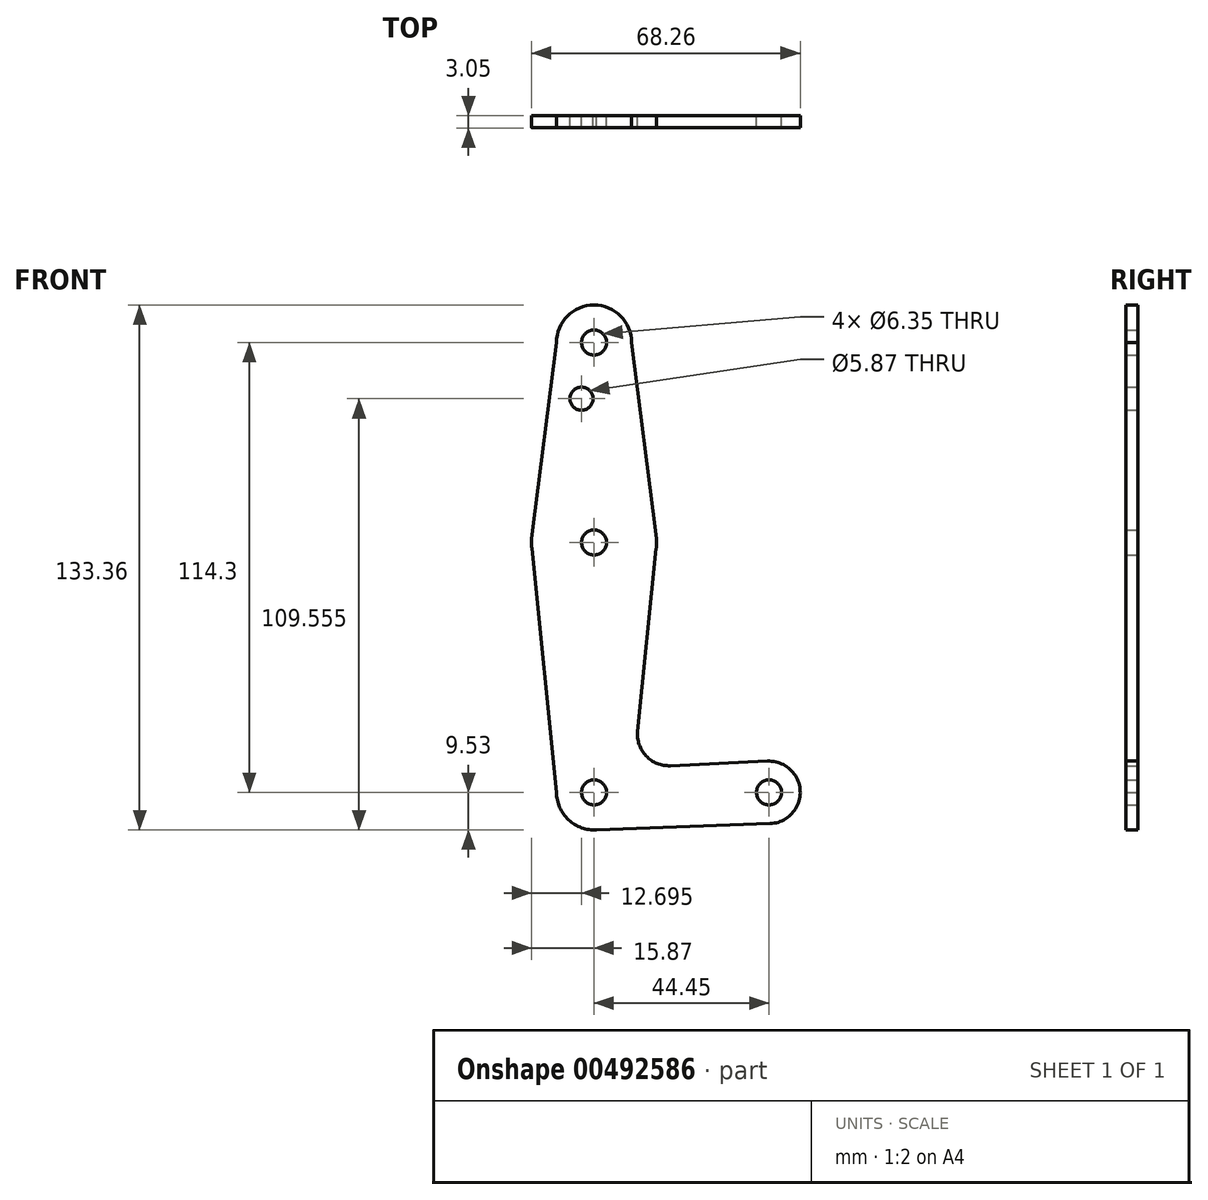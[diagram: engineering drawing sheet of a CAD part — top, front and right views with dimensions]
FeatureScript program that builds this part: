
annotation { "Feature Type Name" : "Feature", "Feature Type Description" : "" }
export const myFeature = defineFeature(function(context is Context, id is Id, definition is map)
    precondition{}
    {
        {
            var Q0;
            Q0=qCreatedBy(makeId("Front.planeOp"),FACE);
            var sketch = newSketch(context, id + "F0", { "sketchPlane" : qUnion([Q0])});
            skLineSegment(sketch, "E0", {"start": v(0, 0) * mm, "end": v(44.45, 0) * mm, "construction": true});
            skCircle(sketch, "E1", {"center": v(0, 0) * mm, "radius": 9.53 * mm});
            skCircle(sketch, "E2", {"center": v(44.45, 0) * mm, "radius": 7.94 * mm});
            skLineSegment(sketch, "E3", {"start": v(0, 0) * mm, "end": v(0, 114.3) * mm, "construction": true});
            skCircle(sketch, "E4", {"center": v(0, 114.3) * mm, "radius": 9.53 * mm});
            skCircle(sketch, "E5", {"center": v(0, 63.5) * mm, "radius": 15.88 * mm});
            skLineSegment(sketch, "E6", {"start": v(0, -9.53) * mm, "end": v(44.73, -7.93) * mm});
            skLineSegment(sketch, "E7", {"start": v(19.38, 6.77) * mm, "end": v(44.08, 7.93) * mm});
            skLineSegment(sketch, "E8", {"start": v(-9.53, 0) * mm, "end": v(-15.8, 61.9) * mm});
            skLineSegment(sketch, "E9", {"start": v(-9.53, 114.3) * mm, "end": v(-15.75, 65.5) * mm});
            skLineSegment(sketch, "E10", {"start": v(9.53, 114.3) * mm, "end": v(15.75, 65.5) * mm});
            skLineSegment(sketch, "E11", {"start": v(11.1, 15.52) * mm, "end": v(15.8, 61.9) * mm});
            skCircle(sketch, "E12", {"center": v(0, 114.3) * mm, "radius": 3.18 * mm});
            skCircle(sketch, "E13", {"center": v(0, 63.5) * mm, "radius": 3.18 * mm});
            skCircle(sketch, "E14", {"center": v(0, 0) * mm, "radius": 3.18 * mm});
            skCircle(sketch, "E15", {"center": v(44.45, 0) * mm, "radius": 3.18 * mm});
            skCircle(sketch, "E16", {"center": v(-3.18, 100.03) * mm, "radius": 2.94 * mm});
            skArc(sketch, "E17.filletArc", {"start": v(11.1, 15.52) * mm, "mid": v(13.23, 9.25) * mm, "end": v(19.38, 6.77) * mm});
            skSolve(sketch);
        }
        {
            var Q0;
            Q0 = qSketchRegion(id + "F0", true);
            extrude(context, id + "F1", {"entities" : qUnion([Q0]), "depth" : 3.05 * mm});
        }
    });
